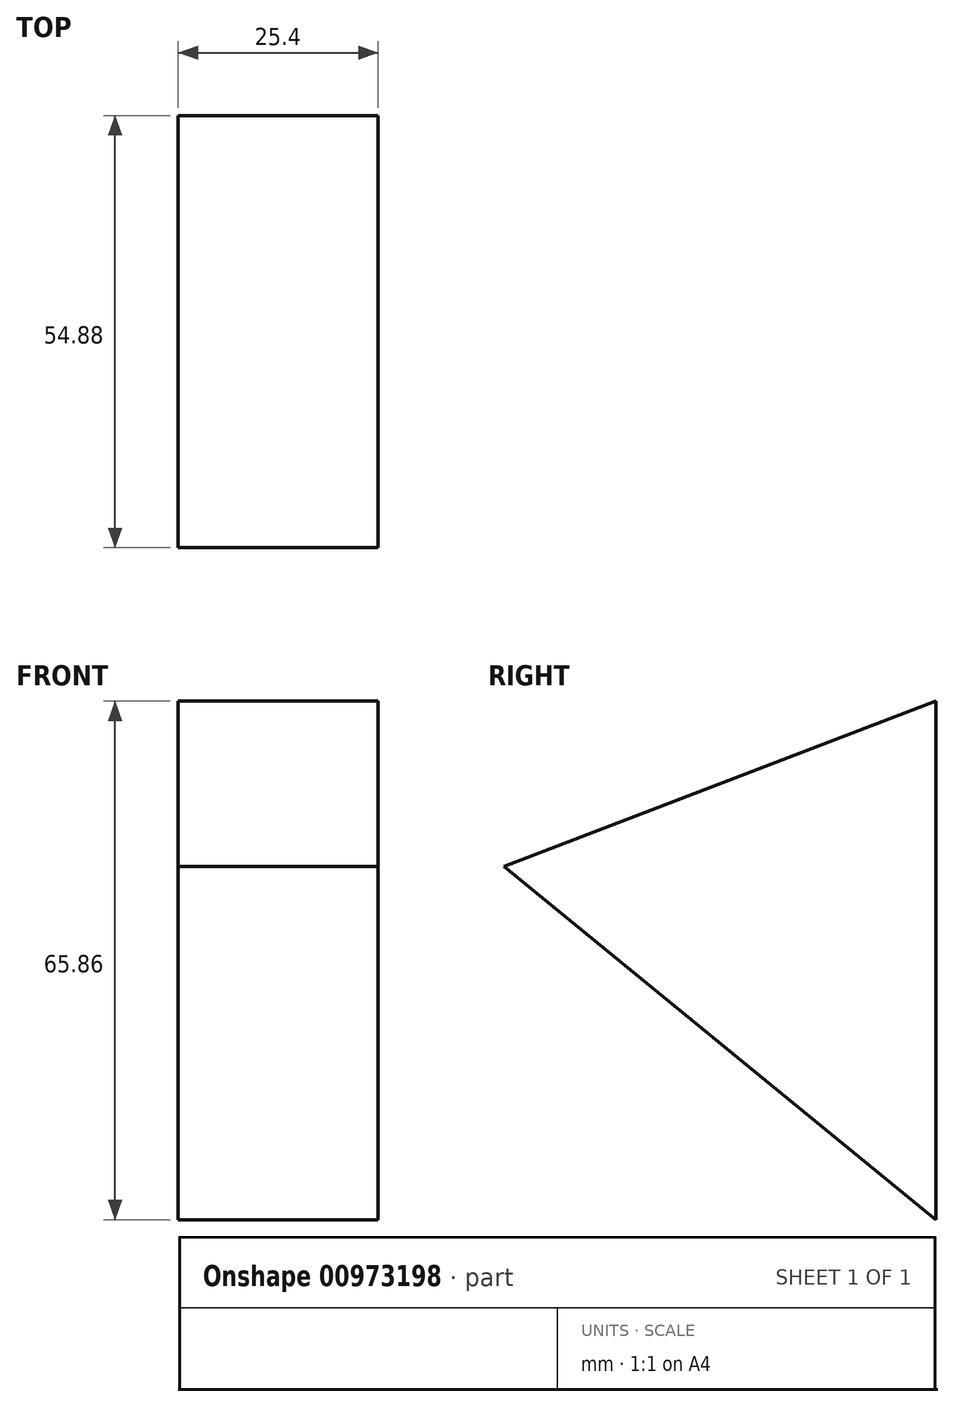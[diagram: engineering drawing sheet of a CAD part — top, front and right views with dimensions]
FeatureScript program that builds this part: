
annotation { "Feature Type Name" : "Feature", "Feature Type Description" : "" }
export const myFeature = defineFeature(function(context is Context, id is Id, definition is map)
    precondition{}
    {
        {
            var Q0;
            Q0=qCreatedBy(makeId("Right.planeOp"),FACE);
            var sketch = newSketch(context, id + "F0", { "sketchPlane" : qUnion([Q0])});
            skLineSegment(sketch, "E0", {"start": v(-21.3, 12.43) * mm, "end": v(33.58, -32.43) * mm});
            skLineSegment(sketch, "E1", {"start": v(33.58, -32.43) * mm, "end": v(33.58, 33.43) * mm});
            skLineSegment(sketch, "E2", {"start": v(33.58, 33.43) * mm, "end": v(-21.3, 12.43) * mm});
            skSolve(sketch);
        }
        {
            var Q0;
            Q0 = qSketchRegion(id + "F0", true);
            extrude(context, id + "F1", {"entities" : qUnion([Q0]), "depth" : 25.4 * mm, "offsetDistance" : 25.4 * mm});
        }
    });
